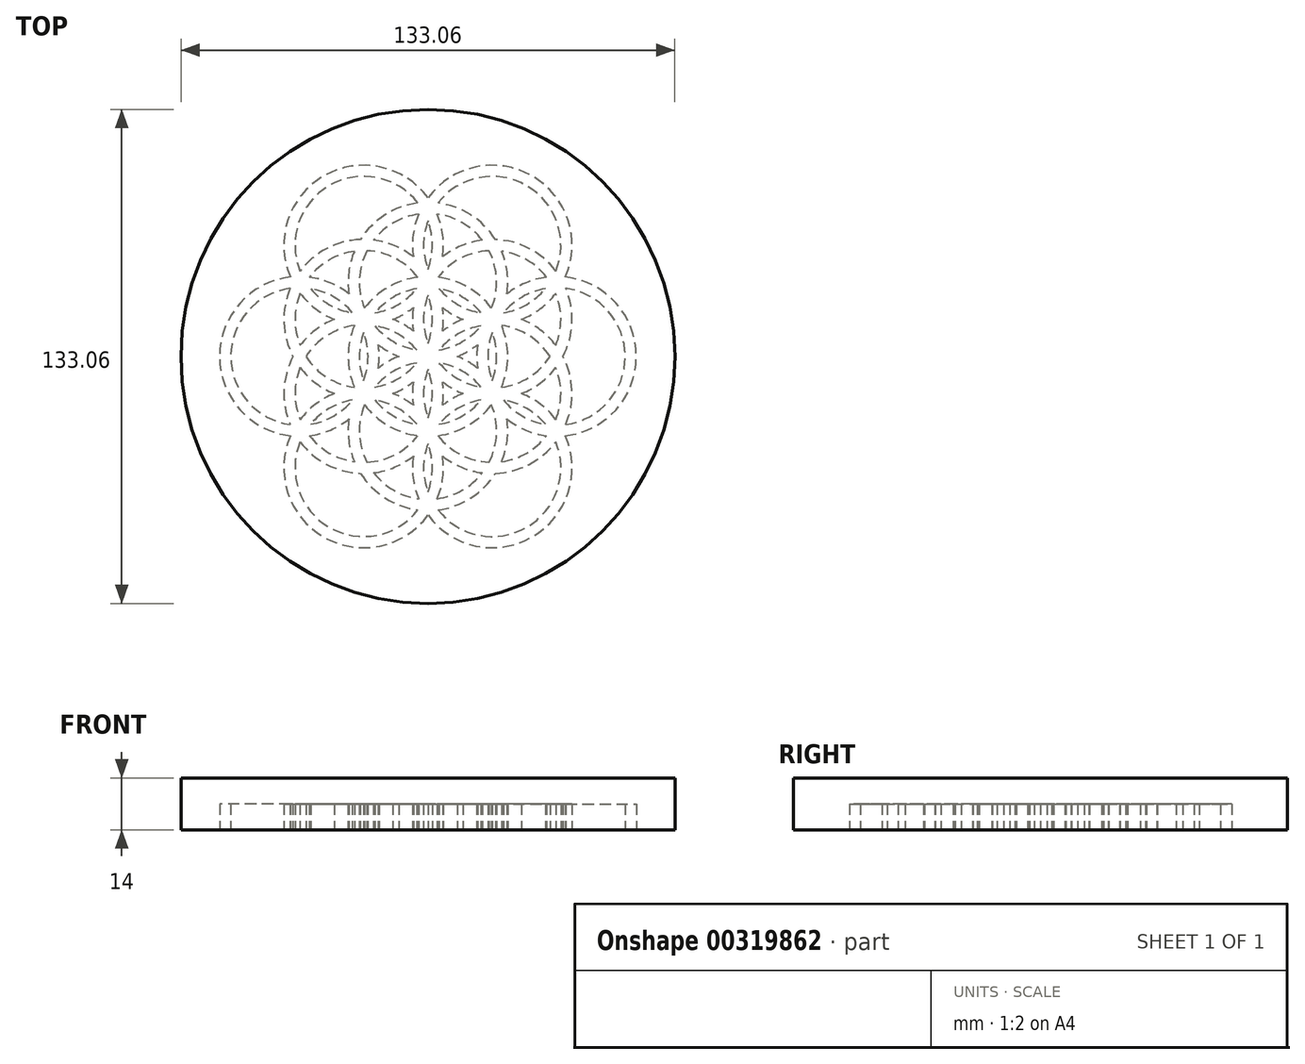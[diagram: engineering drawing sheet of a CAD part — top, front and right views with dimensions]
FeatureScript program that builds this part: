
annotation { "Feature Type Name" : "Feature", "Feature Type Description" : "" }
export const myFeature = defineFeature(function(context is Context, id is Id, definition is map)
    precondition{}
    {
        {
            var Q0;
            Q0=qCreatedBy(makeId("Top.planeOp"),FACE);
            var sketch = newSketch(context, id + "F0", { "sketchPlane" : qUnion([Q0])});
            skCircle(sketch, "E0", {"center": v(0, 20) * mm, "radius": 20 * mm, "construction": true});
            skCircle(sketch, "E1.0", {"center": v(0, 20) * mm, "radius": 21.5 * mm});
            skCircle(sketch, "E2.0", {"center": v(0, 20) * mm, "radius": 18.5 * mm});
            skPoint(sketch, "E3", {"position": v(0, 0) * mm});
            skSolve(sketch);
        }
        {
            var Q0;
            Q0=makeQuery(id+"F0.imprint","IMPRINT",FACE,{"disambiguationData":[TD([[makeQuery(id+"F0.imprint","IMPRINT",EDGE,{"derivedFrom":sQuery(id+"F0.wireOp",EDGE,"E1.0")}),1.0]])]});
            extrude(context, id + "F1", {"entities" : qUnion([Q0]), "depth" : 7 * mm});
        }
        {
            var Q0;
            Q0=qCreatedBy(makeId("Top.planeOp"),FACE);
            var sketch = newSketch(context, id + "F2", { "sketchPlane" : qUnion([Q0])});
            skPoint(sketch, "E4", {"position": v(0, 0) * mm});
            skSolve(sketch);
        }
        {
            var Q0;
            Q0=qCreatedBy(makeId("Right.planeOp"),FACE);
            var sketch = newSketch(context, id + "F3", { "sketchPlane" : qUnion([Q0])});
            skLineSegment(sketch, "E5", {"start": v(0, 0) * mm, "end": v(0, 11.18) * mm});
            skSolve(sketch);
        }
        {
            var Q0;
            Q0=makeQuery(id+"F1.opExtrude","SWEPT_BODY",BODY,{"disambiguationData":[OSD([sQuery(id+"F0.wireOp",EDGE,"E1.0"),sQuery(id+"F0.wireOp",EDGE,"E2.0")])]});
            var Q1;
            Q1=sQuery(id+"F3.wireOp",EDGE,"E5");
            circularPattern(context, id + "F4", {"entities" : qUnion([Q0]), "axis" : qUnion([Q1]), "angle" : 360 * degree, "instanceCount" : 6, "equalSpace" : true});
        }
        {
            var Q0;
            Q0=qCreatedBy(makeId("Top.planeOp"),FACE);
            var sketch = newSketch(context, id + "F5", { "sketchPlane" : qUnion([Q0])});
            skCircle(sketch, "E6", {"center": v(0, 0) * mm, "radius": 20 * mm, "construction": true});
            skCircle(sketch, "E7.0", {"center": v(0, 0) * mm, "radius": 21.5 * mm, "construction": true});
            skCircle(sketch, "E8.0", {"center": v(0, 0) * mm, "radius": 18.5 * mm, "construction": true});
            skCircle(sketch, "E9", {"center": v(0, 20) * mm, "radius": 20 * mm, "construction": true});
            skCircle(sketch, "E10.0", {"center": v(0, 20) * mm, "radius": 21.5 * mm, "construction": true});
            skCircle(sketch, "E11.0", {"center": v(0, 20) * mm, "radius": 18.5 * mm, "construction": true});
            skCircle(sketch, "E12", {"center": v(-17.32, 10) * mm, "radius": 20 * mm, "construction": true});
            skCircle(sketch, "E13.0", {"center": v(-17.32, 10) * mm, "radius": 21.5 * mm, "construction": true});
            skCircle(sketch, "E14.0", {"center": v(-17.32, 10) * mm, "radius": 18.5 * mm, "construction": true});
            skCircle(sketch, "E15", {"center": v(-17.32, 30) * mm, "radius": 20 * mm, "construction": true});
            skCircle(sketch, "E16.0", {"center": v(-17.32, 30) * mm, "radius": 21.5 * mm});
            skCircle(sketch, "E17.0", {"center": v(-17.32, 30) * mm, "radius": 18.5 * mm});
            skSolve(sketch);
        }
        {
            var Q0;
            Q0=qCreatedBy(makeId("Top.planeOp"),FACE);
            var sketch = newSketch(context, id + "F6", { "sketchPlane" : qUnion([Q0])});
            skCircle(sketch, "E18", {"center": v(0, 0) * mm, "radius": 20 * mm, "construction": true});
            skCircle(sketch, "E19.0", {"center": v(0, 0) * mm, "radius": 21.5 * mm});
            skCircle(sketch, "E20.0", {"center": v(0, 0) * mm, "radius": 18.5 * mm});
            skSolve(sketch);
        }
        {
            var Q0;
            Q0 = qSketchRegion(id + "F6", true);
            extrude(context, id + "F7", {"entities" : qUnion([Q0]), "depth" : 7 * mm});
        }
        {
            var Q0;
            Q0 = qSketchRegion(id + "F5", true);
            extrude(context, id + "F8", {"entities" : qUnion([Q0]), "depth" : 7 * mm});
        }
        {
            var Q0;
            Q0=makeQuery(id+"F8.opExtrude","SWEPT_BODY",BODY,{"disambiguationData":[OSD([sQuery(id+"F5.wireOp",EDGE,"E16.0"),sQuery(id+"F5.wireOp",EDGE,"E17.0")])]});
            var Q1;
            Q1=sQuery(id+"F3.wireOp",EDGE,"E5");
            circularPattern(context, id + "F9", {"entities" : qUnion([Q0]), "axis" : qUnion([Q1]), "angle" : 360 * degree, "instanceCount" : 6, "equalSpace" : true});
        }
        {
            var Q0;
            Q0=qCreatedBy(makeId("Top.planeOp"),FACE);
            var sketch = newSketch(context, id + "F10", { "sketchPlane" : qUnion([Q0])});
            skCircle(sketch, "E21", {"center": v(0, 0) * mm, "radius": 66.53 * mm});
            skSolve(sketch);
        }
        {
            var Q0;
            Q0 = qSketchRegion(id + "F10", true);
            extrude(context, id + "F11", {"entities" : qUnion([Q0]), "depth" : 14 * mm});
        }
        {
            var Q0;
            Q0=makeQuery(id+"F1.opExtrude","SWEPT_BODY",BODY,{"disambiguationData":[OSD([sQuery(id+"F0.wireOp",EDGE,"E1.0"),sQuery(id+"F0.wireOp",EDGE,"E2.0")])]});
            var Q1;
            Q1=makeQuery(id+"F4.opPattern","COPY",BODY,{"derivedFrom":makeQuery(id+"F1.opExtrude","SWEPT_BODY",BODY,{"disambiguationData":[OSD([sQuery(id+"F0.wireOp",EDGE,"E1.0"),sQuery(id+"F0.wireOp",EDGE,"E2.0")])]}),"instanceName":"2"});
            var Q2;
            Q2=makeQuery(id+"F4.opPattern","COPY",BODY,{"derivedFrom":makeQuery(id+"F1.opExtrude","SWEPT_BODY",BODY,{"disambiguationData":[OSD([sQuery(id+"F0.wireOp",EDGE,"E1.0"),sQuery(id+"F0.wireOp",EDGE,"E2.0")])]}),"instanceName":"3"});
            var Q3;
            Q3=makeQuery(id+"F4.opPattern","COPY",BODY,{"derivedFrom":makeQuery(id+"F1.opExtrude","SWEPT_BODY",BODY,{"disambiguationData":[OSD([sQuery(id+"F0.wireOp",EDGE,"E1.0"),sQuery(id+"F0.wireOp",EDGE,"E2.0")])]}),"instanceName":"1"});
            var Q4;
            Q4=makeQuery(id+"F4.opPattern","COPY",BODY,{"derivedFrom":makeQuery(id+"F1.opExtrude","SWEPT_BODY",BODY,{"disambiguationData":[OSD([sQuery(id+"F0.wireOp",EDGE,"E1.0"),sQuery(id+"F0.wireOp",EDGE,"E2.0")])]}),"instanceName":"4"});
            var Q5;
            Q5=makeQuery(id+"F4.opPattern","COPY",BODY,{"derivedFrom":makeQuery(id+"F1.opExtrude","SWEPT_BODY",BODY,{"disambiguationData":[OSD([sQuery(id+"F0.wireOp",EDGE,"E1.0"),sQuery(id+"F0.wireOp",EDGE,"E2.0")])]}),"instanceName":"5"});
            var Q6;
            Q6=makeQuery(id+"F7.opExtrude","SWEPT_BODY",BODY,{"disambiguationData":[OSD([sQuery(id+"F6.wireOp",EDGE,"E19.0"),sQuery(id+"F6.wireOp",EDGE,"E20.0")])]});
            var Q7;
            Q7=makeQuery(id+"F9.opPattern","COPY",BODY,{"derivedFrom":makeQuery(id+"F8.opExtrude","SWEPT_BODY",BODY,{"disambiguationData":[OSD([sQuery(id+"F5.wireOp",EDGE,"E16.0"),sQuery(id+"F5.wireOp",EDGE,"E17.0")])]}),"instanceName":"1"});
            var Q8;
            Q8=makeQuery(id+"F8.opExtrude","SWEPT_BODY",BODY,{"disambiguationData":[OSD([sQuery(id+"F5.wireOp",EDGE,"E16.0"),sQuery(id+"F5.wireOp",EDGE,"E17.0")])]});
            var Q9;
            Q9=makeQuery(id+"F9.opPattern","COPY",BODY,{"derivedFrom":makeQuery(id+"F8.opExtrude","SWEPT_BODY",BODY,{"disambiguationData":[OSD([sQuery(id+"F5.wireOp",EDGE,"E16.0"),sQuery(id+"F5.wireOp",EDGE,"E17.0")])]}),"instanceName":"2"});
            var Q10;
            Q10=makeQuery(id+"F9.opPattern","COPY",BODY,{"derivedFrom":makeQuery(id+"F8.opExtrude","SWEPT_BODY",BODY,{"disambiguationData":[OSD([sQuery(id+"F5.wireOp",EDGE,"E16.0"),sQuery(id+"F5.wireOp",EDGE,"E17.0")])]}),"instanceName":"3"});
            var Q11;
            Q11=makeQuery(id+"F9.opPattern","COPY",BODY,{"derivedFrom":makeQuery(id+"F8.opExtrude","SWEPT_BODY",BODY,{"disambiguationData":[OSD([sQuery(id+"F5.wireOp",EDGE,"E16.0"),sQuery(id+"F5.wireOp",EDGE,"E17.0")])]}),"instanceName":"4"});
            var Q12;
            Q12=makeQuery(id+"F9.opPattern","COPY",BODY,{"derivedFrom":makeQuery(id+"F8.opExtrude","SWEPT_BODY",BODY,{"disambiguationData":[OSD([sQuery(id+"F5.wireOp",EDGE,"E16.0"),sQuery(id+"F5.wireOp",EDGE,"E17.0")])]}),"instanceName":"5"});
            var Q13;
            Q13=makeQuery(id+"F11.opExtrude","SWEPT_BODY",BODY,{"disambiguationData":[OSD([sQuery(id+"F10.wireOp",EDGE,"E21")])]});
            booleanBodies(context, id + "F12", {"operationType" : BooleanOperationType.SUBTRACTION, "tools" : qUnion([Q0, Q1, Q2, Q3, Q4, Q5, Q6, Q7, Q8, Q9, Q10, Q11, Q12]), "targets" : qUnion([Q13])});
        }
    });
